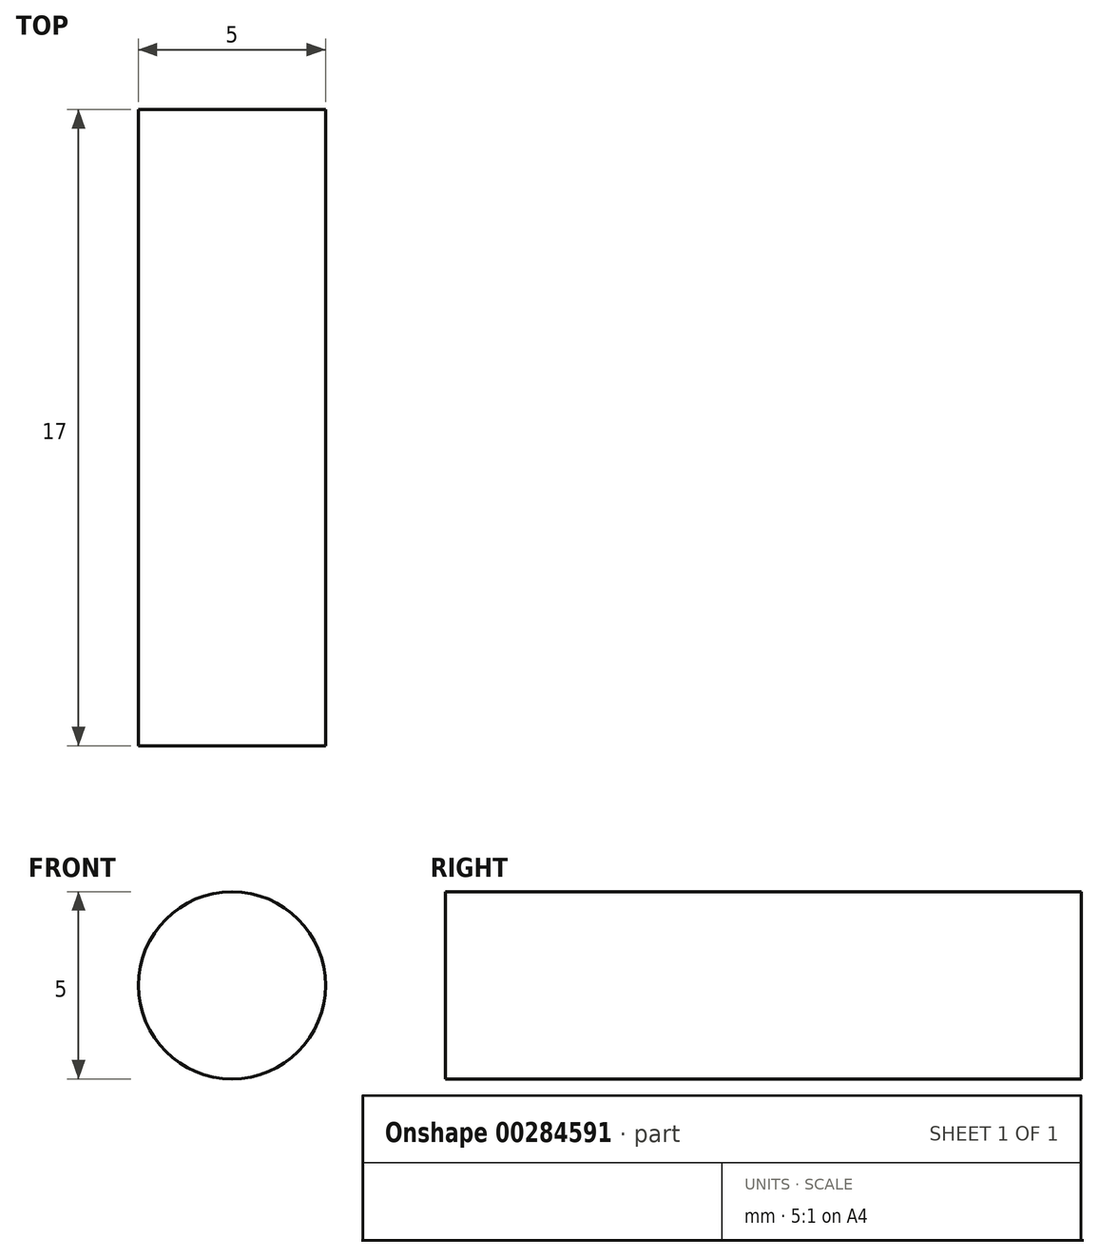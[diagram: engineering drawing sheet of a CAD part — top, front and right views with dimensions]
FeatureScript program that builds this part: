
annotation { "Feature Type Name" : "Feature", "Feature Type Description" : "" }
export const myFeature = defineFeature(function(context is Context, id is Id, definition is map)
    precondition{}
    {
        {
            var Q0;
            Q0=qCreatedBy(makeId("Front.planeOp"),FACE);
            var sketch = newSketch(context, id + "F0", { "sketchPlane" : qUnion([Q0])});
            skCircle(sketch, "E0", {"center": v(0, 0) * mm, "radius": 2.5 * mm});
            skSolve(sketch);
        }
        {
            var Q0;
            Q0=qSketchRegion(id+"F0",true);
            extrude(context, id + "F1", {"entities" : qUnion([Q0]), "depth" : 17 * mm});
        }
    });
